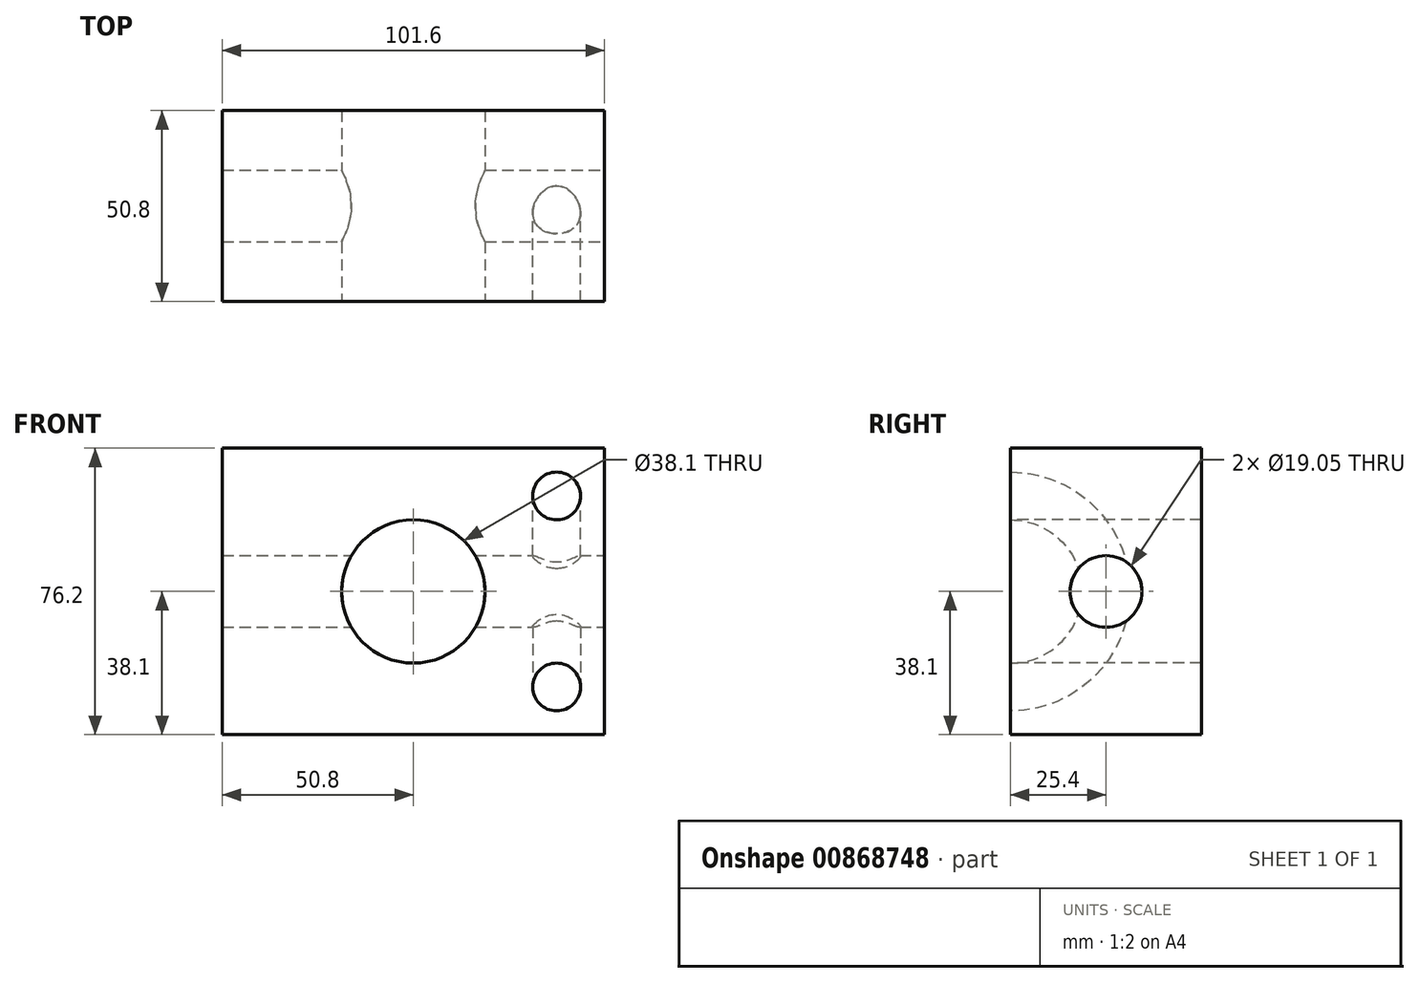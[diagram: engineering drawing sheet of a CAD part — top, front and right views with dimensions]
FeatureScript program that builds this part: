
annotation { "Feature Type Name" : "Feature", "Feature Type Description" : "" }
export const myFeature = defineFeature(function(context is Context, id is Id, definition is map)
    precondition{}
    {
        {
            var Q0;
            Q0=qCreatedBy(makeId("Front.planeOp"),FACE);
            var sketch = newSketch(context, id + "F0", { "sketchPlane" : qUnion([Q0])});
            skLineSegment(sketch, "E0.bottom", {"start": v(0, 0) * mm, "end": v(101.6, 0) * mm});
            skLineSegment(sketch, "E0.top", {"start": v(0, 76.2) * mm, "end": v(101.6, 76.2) * mm});
            skLineSegment(sketch, "E0.left", {"start": v(0, 0) * mm, "end": v(0, 76.2) * mm});
            skLineSegment(sketch, "E0.right", {"start": v(101.6, 0) * mm, "end": v(101.6, 76.2) * mm});
            skSolve(sketch);
        }
        {
            var Q0;
            Q0=makeQuery(id+"F0.imprint","IMPRINT",FACE,{"disambiguationData":[TD([[makeQuery(id+"F0.imprint","IMPRINT",EDGE,{"derivedFrom":sQuery(id+"F0.wireOp",EDGE,"E0.bottom")}),1.0]])]});
            extrude(context, id + "F1", {"entities" : qUnion([Q0]), "depth" : 50.8 * mm, "offsetDistance" : 25.4 * mm});
        }
        {
            var Q0;
            Q0=makeQuery(id+"F1.opExtrude","CAP_FACE",FACE,{"disambiguationData":[OSD([sQuery(id+"F0.wireOp",EDGE,"E0.bottom"),sQuery(id+"F0.wireOp",EDGE,"E0.top"),sQuery(id+"F0.wireOp",EDGE,"E0.left"),sQuery(id+"F0.wireOp",EDGE,"E0.right")])],"isStart":false});
            var sketch = newSketch(context, id + "F2", { "sketchPlane" : qUnion([Q0])});
            skCircle(sketch, "E1", {"center": v(50.8, 38.1) * mm, "radius": 19.05 * mm});
            skLineSegment(sketch, "E2", {"start": v(0, 76.2) * mm, "end": v(101.6, 0) * mm, "construction": true});
            skLineSegment(sketch, "E3", {"start": v(101.6, 76.2) * mm, "end": v(0, 0) * mm, "construction": true});
            skSolve(sketch);
        }
        {
            var Q0;
            Q0=makeQuery(id+"F2.imprint","IMPRINT",FACE,{"disambiguationData":[TD([[makeQuery(id+"F2.imprint","IMPRINT",EDGE,{"derivedFrom":sQuery(id+"F2.wireOp",EDGE,"E1")}),1.0]])]});
            extrude(context, id + "F3", {"entities" : qUnion([Q0]), "operationType" : NewBodyOperationType.REMOVE, "endBound" : BoundingType.THROUGH_ALL, "oppositeDirection" : true, "depth" : 144.27 * mm, "offsetDistance" : 25.4 * mm});
        }
        {
            var Q0;
            Q0=makeQuery(id+"F1.opExtrude","SWEPT_FACE",FACE,{"disambiguationData":[OSD([sQuery(id+"F0.wireOp",EDGE,"E0.right")])]});
            var sketch = newSketch(context, id + "F4", { "sketchPlane" : qUnion([Q0])});
            skLineSegment(sketch, "E4", {"start": v(-50.8, 76.2) * mm, "end": v(0, 0) * mm});
            skCircle(sketch, "E5", {"center": v(-25.4, 38.1) * mm, "radius": 9.53 * mm});
            skSolve(sketch);
        }
        {
            var Q0;
            {var subQ0=sQuery(id+"F4.wireOp",EDGE,"E5");var subQ1=sQuery(id+"F4.wireOp",EDGE,"E4");var subQ2=makeQuery(id+"F4.imprint","INTERSECT",VERTEX,{"disambiguationData":[OD(0.0)],"derivedFrom":[subQ1,subQ0]});Q0=makeQuery(id+"F4.imprint","IMPRINT",FACE,{"disambiguationData":[TD([[makeQuery(id+"F4.imprint","IMPRINT",EDGE,{"disambiguationData":[TD([[subQ2,-1.0]])],"derivedFrom":subQ1}),1.0]])]});}
            var Q1;
            {var subQ0=sQuery(id+"F4.wireOp",EDGE,"E5");var subQ1=sQuery(id+"F4.wireOp",EDGE,"E4");var subQ2=makeQuery(id+"F4.imprint","INTERSECT",VERTEX,{"disambiguationData":[OD(0.0)],"derivedFrom":[subQ1,subQ0]});Q1=makeQuery(id+"F4.imprint","IMPRINT",FACE,{"disambiguationData":[TD([[makeQuery(id+"F4.imprint","IMPRINT",EDGE,{"disambiguationData":[TD([[subQ2,-1.0]])],"derivedFrom":subQ1}),-1.0]])]});}
            extrude(context, id + "F5", {"entities" : qUnion([Q0, Q1]), "operationType" : NewBodyOperationType.REMOVE, "endBound" : BoundingType.THROUGH_ALL, "oppositeDirection" : true, "depth" : 25.4 * mm, "offsetDistance" : 25.4 * mm});
        }
        {
            var Q0;
            Q0=makeQuery(id+"F1.opExtrude","CAP_FACE",FACE,{"disambiguationData":[OSD([sQuery(id+"F0.wireOp",EDGE,"E0.bottom"),sQuery(id+"F0.wireOp",EDGE,"E0.top"),sQuery(id+"F0.wireOp",EDGE,"E0.left"),sQuery(id+"F0.wireOp",EDGE,"E0.right")])],"isStart":false});
            var sketch = newSketch(context, id + "F6", { "sketchPlane" : qUnion([Q0])});
            skCircle(sketch, "E6", {"center": v(88.9, 63.5) * mm, "radius": 6.35 * mm});
            skLineSegment(sketch, "E7", {"start": v(101.6, 38.1) * mm, "end": v(82.08, 38.1) * mm});
            skSolve(sketch);
        }
        {
            var Q0;
            Q0=makeQuery(id+"F6.imprint","IMPRINT",FACE,{"disambiguationData":[TD([[makeQuery(id+"F6.imprint","IMPRINT",EDGE,{"derivedFrom":sQuery(id+"F6.wireOp",EDGE,"E6")}),1.0]])]});
            var Q1;
            Q1=sQuery(id+"F6.wireOp",EDGE,"E7");
            revolve(context, id + "F7", {"operationType" : NewBodyOperationType.REMOVE, "surfaceOperationType" : NewSurfaceOperationType.NEW, "entities" : qUnion([Q0]), "axis" : qUnion([Q1]), "revolveType" : RevolveType.FULL, "oppositeDirection" : true});
        }
    });
